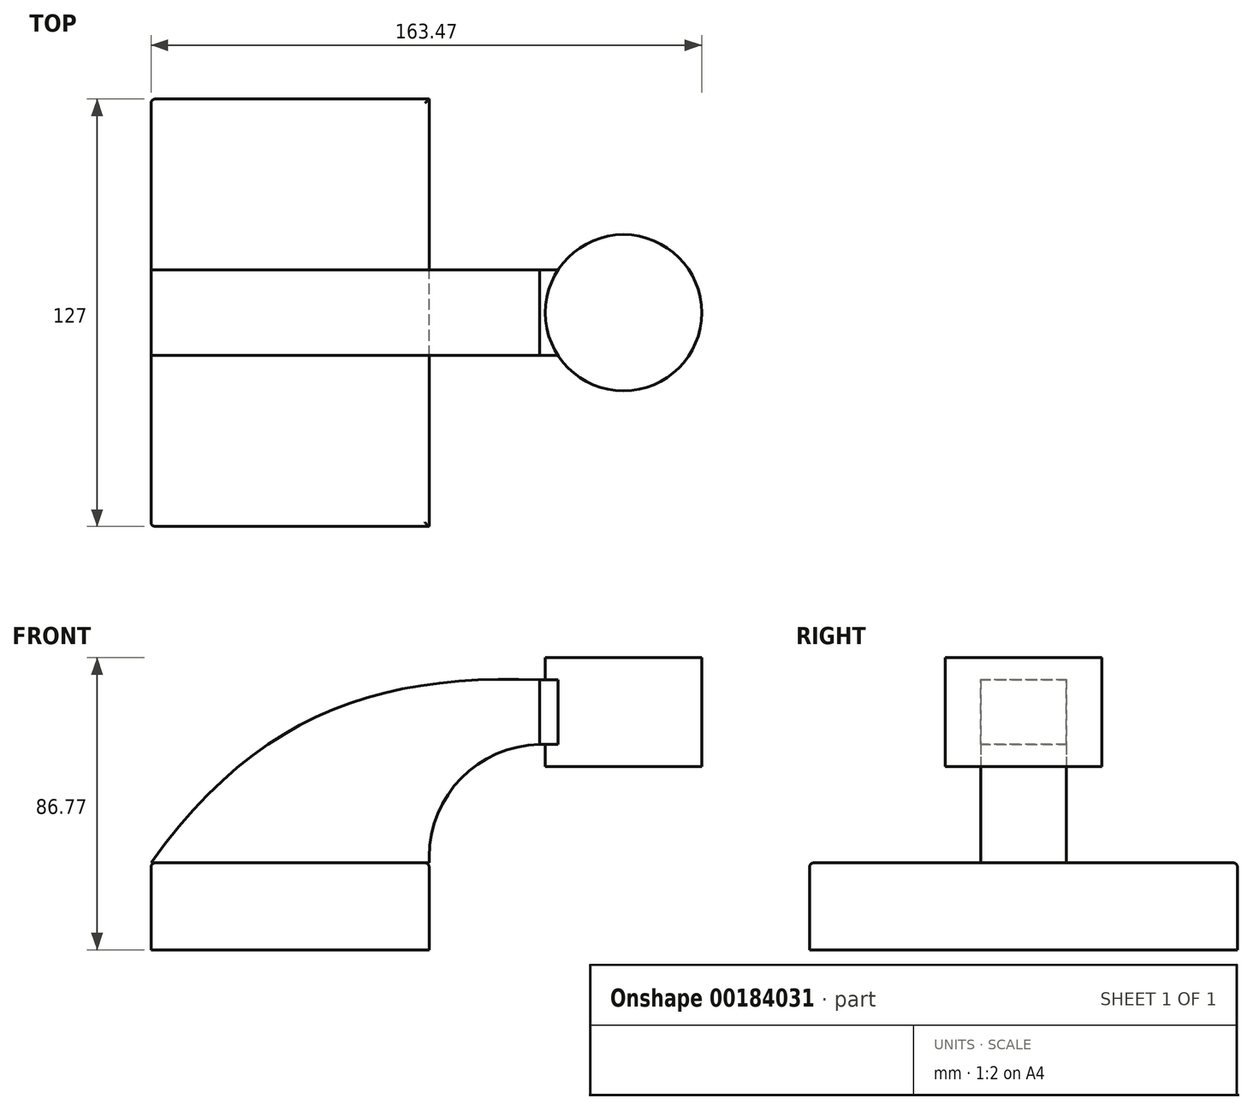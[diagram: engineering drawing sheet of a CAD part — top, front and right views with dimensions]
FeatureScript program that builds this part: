
annotation { "Feature Type Name" : "Feature", "Feature Type Description" : "" }
export const myFeature = defineFeature(function(context is Context, id is Id, definition is map)
    precondition{}
    {
        {
            var Q0;
            Q0=qCreatedBy(makeId("Front.planeOp"),FACE);
            var sketch = newSketch(context, id + "F0", { "sketchPlane" : qUnion([Q0])});
            skLineSegment(sketch, "E0.bottom", {"start": v(41.28, -12.92) * mm, "end": v(-41.28, -12.92) * mm});
            skLineSegment(sketch, "E0.top", {"start": v(41.28, 12.92) * mm, "end": v(-41.28, 12.92) * mm});
            skLineSegment(sketch, "E0.left", {"start": v(41.28, 12.92) * mm, "end": v(41.28, -12.92) * mm});
            skLineSegment(sketch, "E0.right", {"start": v(-41.28, 12.92) * mm, "end": v(-41.28, -12.92) * mm});
            skPoint(sketch, "E0.middle", {"position": v(0, 0) * mm});
            skLineSegment(sketch, "E1.bottom", {"start": v(122.19, 41.52) * mm, "end": v(74.03, 41.52) * mm});
            skLineSegment(sketch, "E1.top", {"start": v(122.19, 73.85) * mm, "end": v(74.03, 73.85) * mm});
            skLineSegment(sketch, "E1.left", {"start": v(122.19, 41.52) * mm, "end": v(122.19, 73.85) * mm});
            skLineSegment(sketch, "E1.right", {"start": v(74.03, 41.52) * mm, "end": v(74.03, 73.85) * mm});
            skPoint(sketch, "E1.middle", {"position": v(98.1, 57.69) * mm});
            skLineSegment(sketch, "E2", {"start": v(41.27, -12.92) * mm, "end": v(41.27, 14.74) * mm});
            skArc(sketch, "E3", {"start": v(41.27, 14.74) * mm, "mid": v(51.03, 38.3) * mm, "end": v(74.6, 48.06) * mm});
            skLineSegment(sketch, "E4", {"start": v(74.6, 48.06) * mm, "end": v(98.97, 48.06) * mm});
            skLineSegment(sketch, "E5.0", {"start": v(74.6, 67.24) * mm, "end": v(98.97, 67.24) * mm});
            skArc(sketch, "E5.1", {"start": v(22.1, 14.74) * mm, "mid": v(37.47, 51.87) * mm, "end": v(74.6, 67.24) * mm});
            skLineSegment(sketch, "E5.2", {"start": v(22.1, 14.01) * mm, "end": v(22.1, 14.74) * mm});
            skLineSegment(sketch, "E6", {"start": v(98.97, 41.52) * mm, "end": v(98.97, 48.06) * mm});
            skLineSegment(sketch, "E7", {"start": v(98.97, 67.24) * mm, "end": v(98.97, 48.06) * mm});
            skLineSegment(sketch, "E8", {"start": v(98.97, 67.24) * mm, "end": v(98.97, 73.85) * mm});
            skFitSpline(sketch, "E9", {"points": [v(74.6, 67.24) * mm, v(-41.28, 12.92) * mm], "startDerivative": vector(-144.9, 6.08) * mm, "endDerivative": vector(-94.55, -132.67) * mm});
            skSolve(sketch);
        }
        {
            var Q0;
            {var subQ0=sQuery(id+"F0.wireOp",EDGE,"E0.bottom");Q0=makeQuery(id+"F0.imprint","IMPRINT",FACE,{"disambiguationData":[TD([[makeQuery(id+"F0.imprint","IMPRINT",EDGE,{"derivedFrom":subQ0}),-1.0]])]});}
            extrude(context, id + "F1", {"entities" : qUnion([Q0]), "endBound" : BoundingType.SYMMETRIC, "depth" : 127 * mm});
        }
        {
            var Q0;
            {var subQ1=sQuery(id+"F0.wireOp",EDGE,"E4");Q0=makeQuery(id+"F0.imprint","IMPRINT",FACE,{"disambiguationData":[TD([[makeQuery(id+"F0.imprint","IMPRINT",EDGE,{"derivedFrom":subQ1}),1.0]])]});}
            extrude(context, id + "F2", {"entities" : qUnion([Q0]), "endBound" : BoundingType.SYMMETRIC, "depth" : 25.4 * mm});
        }
        {
            var Q0;
            {var subQ1=sQuery(id+"F0.wireOp",EDGE,"E0.top");Q0=makeQuery(id+"F0.imprint","IMPRINT",FACE,{"disambiguationData":[TD([[makeQuery(id+"F0.imprint","IMPRINT",EDGE,{"derivedFrom":subQ1}),-1.0]])]});}
            extrude(context, id + "F3", {"entities" : qUnion([Q0]), "endBound" : BoundingType.SYMMETRIC, "depth" : 25.4 * mm});
        }
        {
            var Q0;
            {var subQ1=sQuery(id+"F0.wireOp",EDGE,"E1.left");Q0=makeQuery(id+"F0.imprint","IMPRINT",FACE,{"disambiguationData":[TD([[makeQuery(id+"F0.imprint","IMPRINT",EDGE,{"derivedFrom":subQ1}),1.0]])]});}
            var Q1;
            Q1=sQuery(id+"F0.wireOp",EDGE,"E7");
            revolve(context, id + "F4", {"operationType" : NewBodyOperationType.ADD, "entities" : qUnion([Q0]), "axis" : qUnion([Q1]), "revolveType" : RevolveType.FULL});
        }
        {
            var Q0;
            Q0=makeQuery(id+"F1.opExtrude","CAP_EDGE",EDGE,{"disambiguationData":[OSD([sQuery(id+"F0.wireOp",EDGE,"E2")])],"isStart":false});
            var Q1;
            Q1=makeQuery(id+"F1.opExtrude","CAP_EDGE",EDGE,{"disambiguationData":[OSD([sQuery(id+"F0.wireOp",EDGE,"E0.right")])],"isStart":false});
            var Q2;
            Q2=makeQuery(id+"F1.opExtrude","CAP_EDGE",EDGE,{"disambiguationData":[OSD([sQuery(id+"F0.wireOp",EDGE,"E2")])],"isStart":true});
            var Q3;
            Q3=makeQuery(id+"F1.opExtrude","CAP_EDGE",EDGE,{"disambiguationData":[OSD([sQuery(id+"F0.wireOp",EDGE,"E0.right")])],"isStart":true});
            var Q4;
            Q4=makeQuery(id+"F1.opExtrude","CAP_EDGE",EDGE,{"disambiguationData":[OSD([sQuery(id+"F0.wireOp",EDGE,"E0.top")])],"isStart":true});
            var Q5;
            Q5=makeQuery(id+"F1.opExtrude","CAP_EDGE",EDGE,{"disambiguationData":[OSD([sQuery(id+"F0.wireOp",EDGE,"E0.top")])],"isStart":false});
            var Q6;
            Q6=makeQuery(id+"F1.opExtrude","SWEPT_EDGE",EDGE,{"disambiguationData":[OSD([sQuery(id+"F0.wireOp",EDGE,"E0.top"),sQuery(id+"F0.wireOp",EDGE,"E0.right"),sQuery(id+"F0.wireOp",EDGE,"E9")])]});
            var Q7;
            Q7=makeQuery(id+"F1.opExtrude","SWEPT_EDGE",EDGE,{"disambiguationData":[OSD([sQuery(id+"F0.wireOp",EDGE,"E0.top"),sQuery(id+"F0.wireOp",EDGE,"E2")])]});
            fillet(context, id + "F5", {"entities" : qUnion([Q0, Q1, Q2, Q3, Q4, Q5, Q6, Q7]), "radius" : 1.27 * mm, "tangentPropagation" : true, "allowEdgeOverflow" : false});
        }
    });
